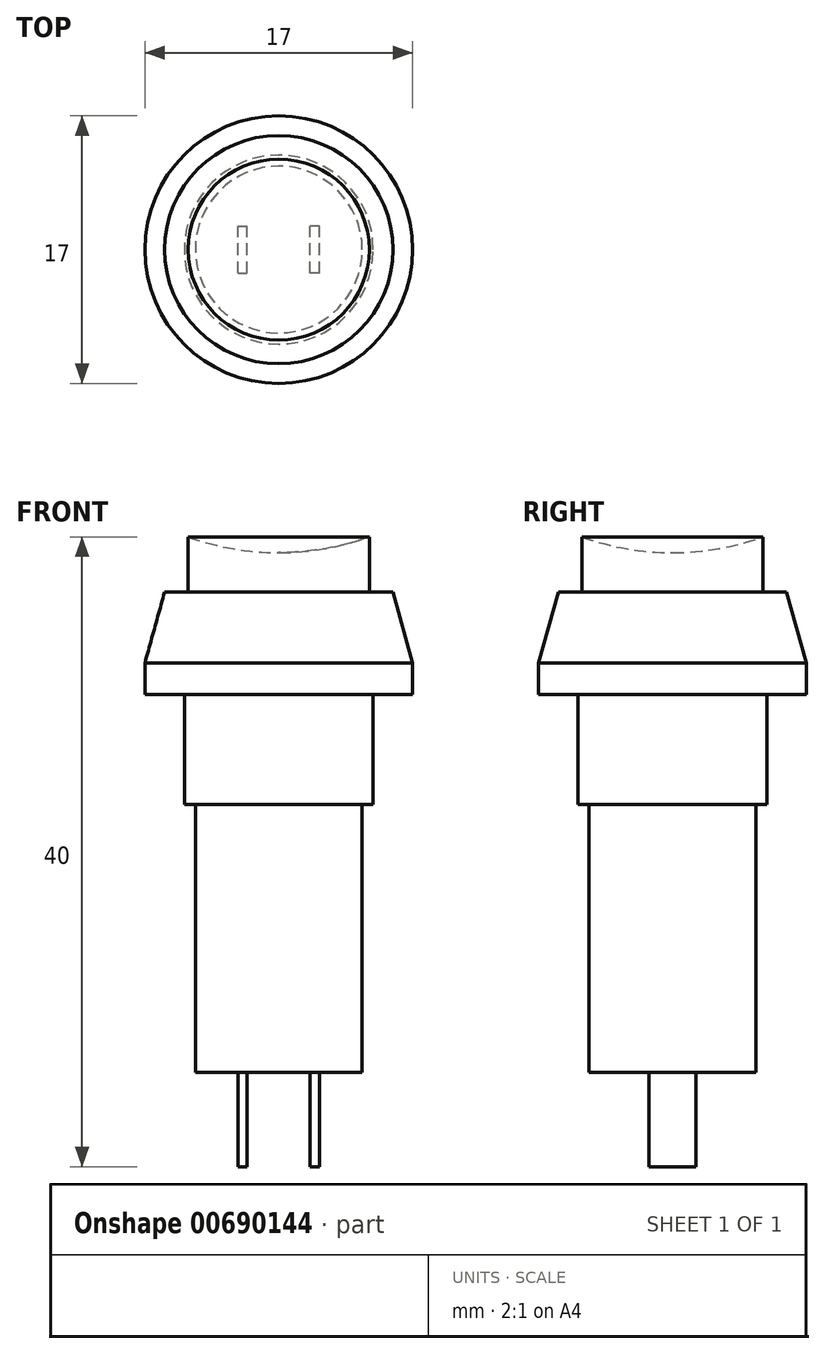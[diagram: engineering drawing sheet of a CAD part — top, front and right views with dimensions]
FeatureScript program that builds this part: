
annotation { "Feature Type Name" : "Feature", "Feature Type Description" : "" }
export const myFeature = defineFeature(function(context is Context, id is Id, definition is map)
    precondition{}
    {
        {
            var Q0;
            Q0=qCreatedBy(makeId("Front.planeOp"),FACE);
            var sketch = newSketch(context, id + "F0", { "sketchPlane" : qUnion([Q0])});
            skLineSegment(sketch, "E0", {"start": v(5.75, 10) * mm, "end": v(5.75, 6.5) * mm});
            skLineSegment(sketch, "E1", {"start": v(5.75, 6.5) * mm, "end": v(7.25, 6.5) * mm});
            skLineSegment(sketch, "E2", {"start": v(7.25, 6.5) * mm, "end": v(8.5, 2) * mm});
            skLineSegment(sketch, "E3", {"start": v(8.5, 2) * mm, "end": v(8.5, 0) * mm});
            skLineSegment(sketch, "E4", {"start": v(8.5, 0) * mm, "end": v(6, 0) * mm});
            skLineSegment(sketch, "E5", {"start": v(6, 0) * mm, "end": v(6, -7) * mm});
            skLineSegment(sketch, "E6", {"start": v(6, -7) * mm, "end": v(5.3, -7) * mm});
            skLineSegment(sketch, "E7", {"start": v(5.3, -7) * mm, "end": v(5.3, -24) * mm});
            skLineSegment(sketch, "E8", {"start": v(5.3, -24) * mm, "end": v(0, -24) * mm});
            skLineSegment(sketch, "E9", {"start": v(0, -24) * mm, "end": v(0, 9) * mm});
            skArc(sketch, "E10", {"start": v(0, 9) * mm, "mid": v(2.92, 9.25) * mm, "end": v(5.75, 10) * mm});
            skLineSegment(sketch, "E11.bottom", {"start": v(2.6, -30) * mm, "end": v(2, -30) * mm});
            skLineSegment(sketch, "E11.top", {"start": v(2.6, -24) * mm, "end": v(2, -24) * mm});
            skLineSegment(sketch, "E11.left", {"start": v(2.6, -30) * mm, "end": v(2.6, -24) * mm});
            skLineSegment(sketch, "E11.right", {"start": v(2, -30) * mm, "end": v(2, -24) * mm});
            skLineSegment(sketch, "E12.MirrorCS", {"start": v(-2.6, -30) * mm, "end": v(-2, -30) * mm});
            skLineSegment(sketch, "E13.MirrorCS", {"start": v(-2.6, -24) * mm, "end": v(-2, -24) * mm});
            skLineSegment(sketch, "E14.MirrorCS", {"start": v(-2.6, -30) * mm, "end": v(-2.6, -24) * mm});
            skLineSegment(sketch, "E15.MirrorCS", {"start": v(-2, -30) * mm, "end": v(-2, -24) * mm});
            skSolve(sketch);
        }
        {
            var Q0;
            Q0=makeQuery(id+"F0.imprint","IMPRINT",FACE,{"disambiguationData":[TD([[makeQuery(id+"F0.imprint","IMPRINT",EDGE,{"derivedFrom":sQuery(id+"F0.wireOp",EDGE,"E0")}),-1.0]])]});
            var Q1;
            Q1 = qConstructionFilter(qBodyType(qCreatedBy(id + "F0" ,EDGE), BodyType.WIRE), ConstructionObject.NO);
            var Q2;
            Q2=sQuery(id+"F0.wireOp",EDGE,"E9");
            revolve(context, id + "F1", {"surfaceOperationType" : NewSurfaceOperationType.NEW, "entities" : qUnion([Q0]), "surfaceEntities" : qUnion([Q1]), "axis" : qUnion([Q2]), "revolveType" : RevolveType.FULL});
        }
        {
            var Q0;
            Q0=makeQuery(id+"F0.imprint","IMPRINT",FACE,{"disambiguationData":[TD([[makeQuery(id+"F0.imprint","IMPRINT",EDGE,{"derivedFrom":sQuery(id+"F0.wireOp",EDGE,"E12.MirrorCS")}),1.0]])]});
            var Q1;
            Q1=makeQuery(id+"F0.imprint","IMPRINT",FACE,{"disambiguationData":[TD([[makeQuery(id+"F0.imprint","IMPRINT",EDGE,{"derivedFrom":sQuery(id+"F0.wireOp",EDGE,"E11.bottom")}),-1.0]])]});
            extrude(context, id + "F2", {"entities" : qUnion([Q0, Q1]), "operationType" : NewBodyOperationType.ADD, "endBound" : BoundingType.SYMMETRIC, "depth" : 3 * mm, "offsetDistance" : 25 * mm});
        }
    });
